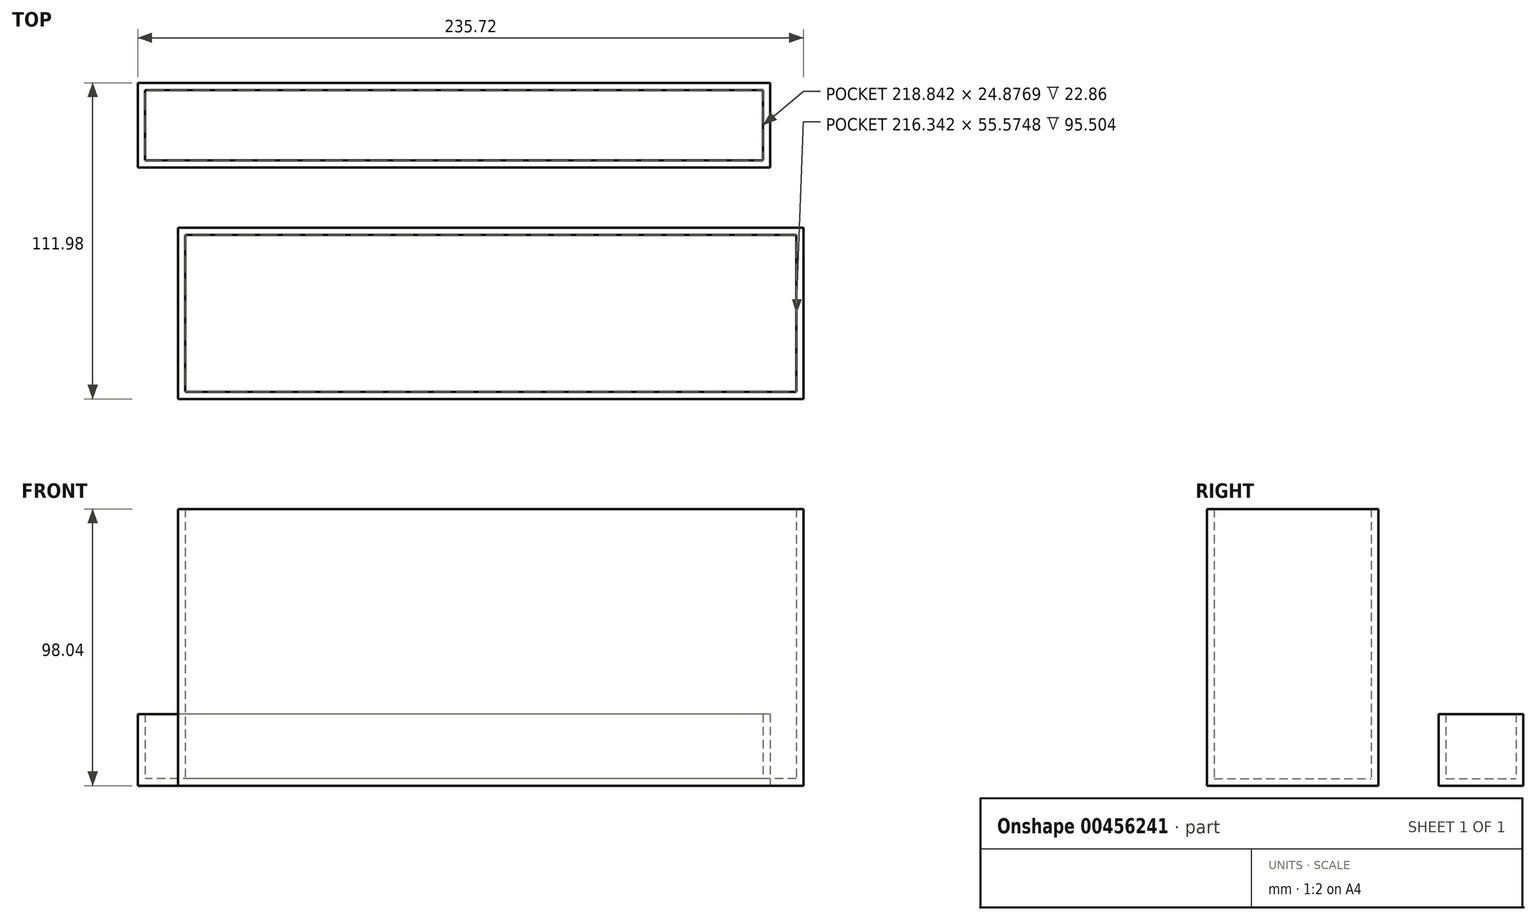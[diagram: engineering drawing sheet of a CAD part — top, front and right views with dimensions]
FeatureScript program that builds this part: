
annotation { "Feature Type Name" : "Feature", "Feature Type Description" : "" }
export const myFeature = defineFeature(function(context is Context, id is Id, definition is map)
    precondition{}
    {
        {
            var Q0;
            Q0=qCreatedBy(makeId("Top.planeOp"),FACE);
            var sketch = newSketch(context, id + "F0", { "sketchPlane" : qUnion([Q0])});
            skLineSegment(sketch, "E0.bottom", {"start": v(0, -126.68) * mm, "end": v(-221.42, -126.68) * mm});
            skLineSegment(sketch, "E0.top", {"start": v(0, -66.03) * mm, "end": v(-221.42, -66.03) * mm});
            skLineSegment(sketch, "E0.left", {"start": v(0, -126.68) * mm, "end": v(0, -66.03) * mm});
            skLineSegment(sketch, "E0.right", {"start": v(-221.42, -126.68) * mm, "end": v(-221.42, -66.03) * mm});
            skPoint(sketch, "E0.middle", {"position": v(-110.71, -96.35) * mm});
            skSolve(sketch);
        }
        {
            var Q0;
            Q0 = qSketchRegion(id + "F0", true);
            extrude(context, id + "F1", {"entities" : qUnion([Q0]), "depth" : 98.04 * mm});
        }
        {
            var Q0;
            Q0=makeQuery(id+"F1.opExtrude","CAP_FACE",FACE,{"disambiguationData":[OSD([sQuery(id+"F0.wireOp",EDGE,"E0.bottom"),sQuery(id+"F0.wireOp",EDGE,"E0.top"),sQuery(id+"F0.wireOp",EDGE,"E0.left"),sQuery(id+"F0.wireOp",EDGE,"E0.right")])],"isStart":false});
            shell(context, id + "F2", {"entities" : qUnion([Q0]), "thickness" : 2.54 * mm});
        }
        {
            var Q0;
            Q0=qCreatedBy(makeId("Top.planeOp"),FACE);
            var sketch = newSketch(context, id + "F3", { "sketchPlane" : qUnion([Q0])});
            skCircle(sketch, "E1", {"center": v(115.48, 56.67) * mm, "radius": 94.6 * mm});
            skSolve(sketch);
        }
        {
            var Q0;
            Q0 = qSketchRegion(id + "F3", true);
            extrude(context, id + "F4", {"entities" : qUnion([Q0]), "operationType" : NewBodyOperationType.REMOVE, "depth" : 230.63 * mm});
        }
        {
            var Q0;
            Q0=qCreatedBy(makeId("Top.planeOp"),FACE);
            var sketch = newSketch(context, id + "F5", { "sketchPlane" : qUnion([Q0])});
            skLineSegment(sketch, "E2.bottom", {"start": v(-132.59, -44.66) * mm, "end": v(-235.72, -44.66) * mm});
            skLineSegment(sketch, "E2.top", {"start": v(-132.59, -14.7) * mm, "end": v(-235.72, -14.7) * mm});
            skLineSegment(sketch, "E2.left", {"start": v(-132.59, -44.66) * mm, "end": v(-132.59, -14.7) * mm});
            skLineSegment(sketch, "E2.right", {"start": v(-235.72, -44.66) * mm, "end": v(-235.72, -14.7) * mm});
            skLineSegment(sketch, "E3.bottom", {"start": v(-132.59, -44.66) * mm, "end": v(-11.8, -44.66) * mm});
            skLineSegment(sketch, "E3.top", {"start": v(-132.59, -14.7) * mm, "end": v(-11.8, -14.7) * mm});
            skLineSegment(sketch, "E3.right", {"start": v(-11.8, -44.66) * mm, "end": v(-11.8, -14.7) * mm});
            skSolve(sketch);
        }
        {
            var Q0;
            Q0 = qSketchRegion(id + "F5", true);
            extrude(context, id + "F6", {"entities" : qUnion([Q0]), "depth" : 25.4 * mm});
        }
        {
            var Q0;
            Q0=makeQuery(id+"F6.opExtrude","CAP_FACE",FACE,{"disambiguationData":[OSD([sQuery(id+"F5.wireOp",EDGE,"E2.bottom"),sQuery(id+"F5.wireOp",EDGE,"E2.top"),sQuery(id+"F5.wireOp",EDGE,"E2.right"),sQuery(id+"F5.wireOp",EDGE,"E3.bottom"),sQuery(id+"F5.wireOp",EDGE,"E3.top"),sQuery(id+"F5.wireOp",EDGE,"E3.right")])],"isStart":false});
            shell(context, id + "F7", {"entities" : qUnion([Q0]), "thickness" : 2.54 * mm});
        }
    });
